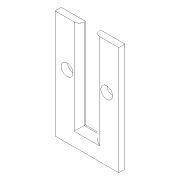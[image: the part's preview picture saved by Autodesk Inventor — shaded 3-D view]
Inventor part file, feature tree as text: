
AUTODESK INVENTOR PART (.ipt)
format: ipt  version: 2022 (Build 260153000, 153)  size: 102,400 bytes
history: native  units: mm
features: extrude x1, fillet x1, sketch x1
ambient origin geometry x8: Origin, YZ Plane, XZ Plane, XY Plane, X Axis, Y Axis, Z Axis, Center Point
bodies: Solid1 (feature_tree)
feature tree (3):
  extrude  "Extrusion1"  Depth=14.5mm
  fillet  "Fillet1"  Radius=2.5mm
  sketch  "Sketch1"  dims[d0=10.3mm d1=14.5mm d2=2.5mm d3=3.0mm d4=3.9mm d5=0.0mm d6=1.9mm d7=1.95mm d8=7.25mm d9=1.9mm d10=1.95mm d11=7.25mm d12=1.0mm d13=0.0mm d14=0.8mm]
